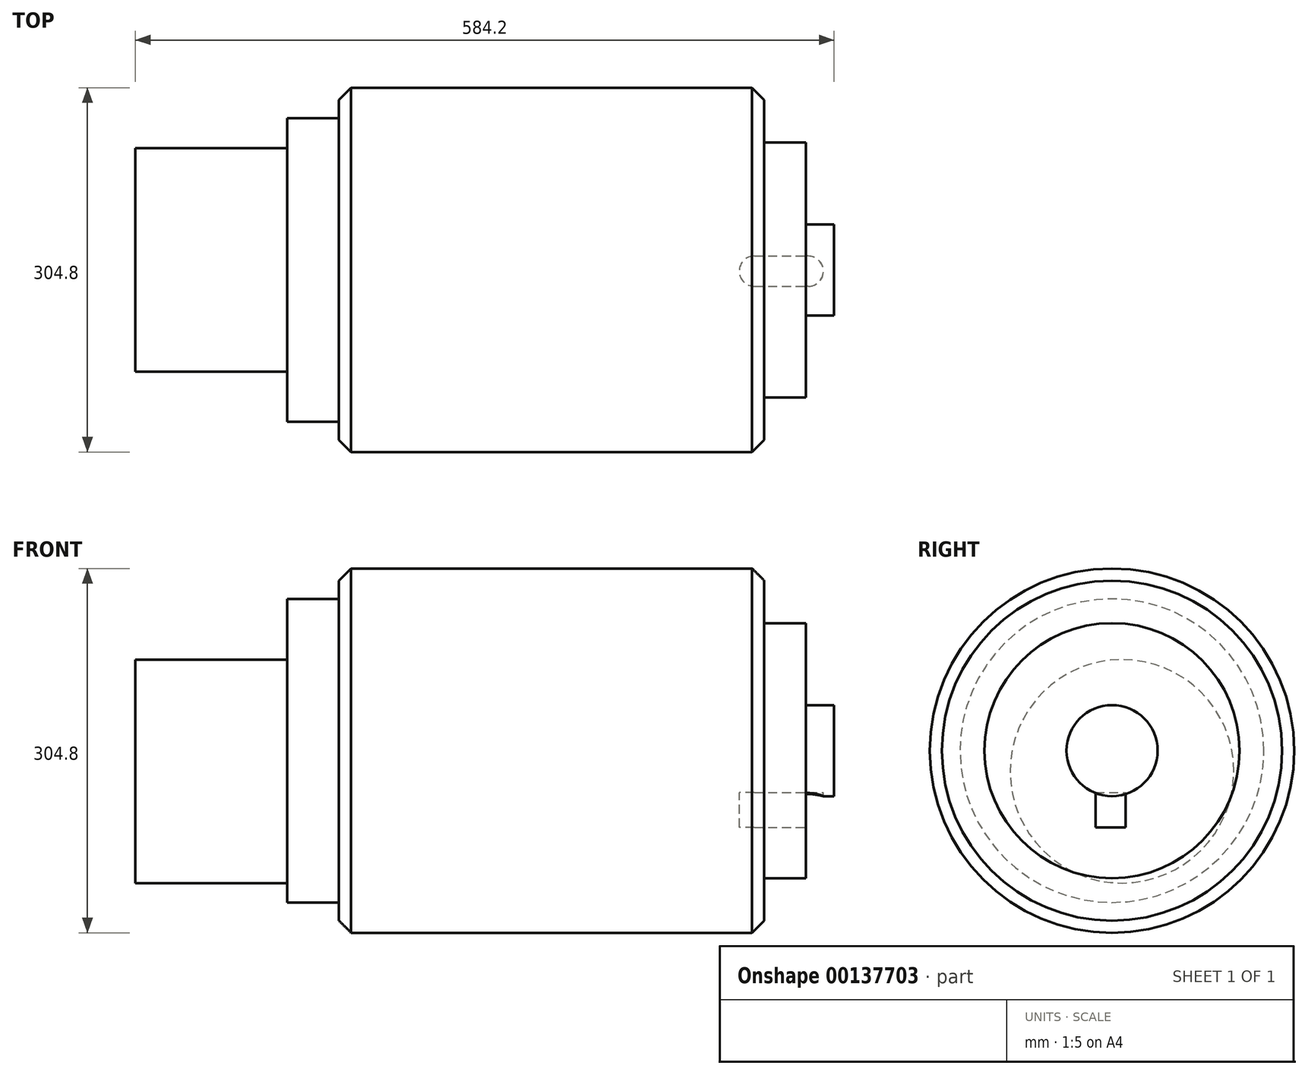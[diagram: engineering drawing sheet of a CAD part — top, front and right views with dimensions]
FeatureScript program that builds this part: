
annotation { "Feature Type Name" : "Feature", "Feature Type Description" : "" }
export const myFeature = defineFeature(function(context is Context, id is Id, definition is map)
    precondition{}
    {
        {
            var Q0;
            Q0=qCreatedBy(makeId("Front.planeOp"),FACE);
            var sketch = newSketch(context, id + "F0", { "sketchPlane" : qUnion([Q0])});
            skLineSegment(sketch, "E0", {"start": v(0, 0) * mm, "end": v(457.2, 0) * mm});
            skLineSegment(sketch, "E1", {"start": v(457.2, 0) * mm, "end": v(457.2, 38.1) * mm});
            skLineSegment(sketch, "E2", {"start": v(457.2, 38.1) * mm, "end": v(433.52, 38.1) * mm});
            skLineSegment(sketch, "E3", {"start": v(433.52, 38.1) * mm, "end": v(433.52, 106.68) * mm});
            skLineSegment(sketch, "E4", {"start": v(433.52, 106.68) * mm, "end": v(398.78, 106.68) * mm});
            skLineSegment(sketch, "E5", {"start": v(398.78, 106.68) * mm, "end": v(398.78, 152.4) * mm});
            skLineSegment(sketch, "E6", {"start": v(398.78, 152.4) * mm, "end": v(43.18, 152.4) * mm});
            skLineSegment(sketch, "E7", {"start": v(43.18, 152.4) * mm, "end": v(43.18, 127) * mm});
            skLineSegment(sketch, "E8", {"start": v(43.18, 127) * mm, "end": v(0, 127) * mm});
            skLineSegment(sketch, "E9", {"start": v(0, 127) * mm, "end": v(0, 0) * mm});
            skSolve(sketch);
        }
        {
            var Q0;
            Q0=makeQuery(id+"F0.imprint","IMPRINT",FACE,{"disambiguationData":[TD([[makeQuery(id+"F0.imprint","IMPRINT",EDGE,{"derivedFrom":sQuery(id+"F0.wireOp",EDGE,"E0")}),1.0]])]});
            var Q1;
            Q1=sQuery(id+"F0.wireOp",EDGE,"E0");
            revolve(context, id + "F1", {"entities" : qUnion([Q0]), "axis" : qUnion([Q1]), "revolveType" : RevolveType.FULL});
        }
        {
            var Q0;
            Q0=qCreatedBy(makeId("Top.planeOp"),FACE);
            var sketch = newSketch(context, id + "F2", { "sketchPlane" : qUnion([Q0])});
            skLineSegment(sketch, "E10", {"start": v(390.59, 11.49) * mm, "end": v(435.6, 11.49) * mm});
            skArc(sketch, "E11", {"start": v(435.6, 11.49) * mm, "mid": v(448.27, -1.17) * mm, "end": v(435.6, -13.83) * mm});
            skArc(sketch, "E12", {"start": v(390.59, 11.49) * mm, "mid": v(377.93, -1.17) * mm, "end": v(390.59, -13.83) * mm});
            skLineSegment(sketch, "E13", {"start": v(390.59, -13.83) * mm, "end": v(435.6, -13.83) * mm});
            skSolve(sketch);
        }
        {
            var Q0;
            Q0 = qSketchRegion(id + "F2", true);
            extrude(context, id + "F3", {"entities" : qUnion([Q0]), "operationType" : NewBodyOperationType.REMOVE, "oppositeDirection" : true, "depth" : 64.26 * mm, "hasSecondDirection" : true, "secondDirectionOppositeDirection" : true, "secondDirectionDepth" : 35.13 * mm});
        }
        {
            var Q0;
            Q0=makeQuery(id+"F1.opRevolve","SWEPT_EDGE",EDGE,{"disambiguationData":[OSD([sQuery(id+"F0.wireOp",EDGE,"E6"),sQuery(id+"F0.wireOp",EDGE,"E7")])]});
            var Q1;
            Q1=makeQuery(id+"F1.opRevolve","SWEPT_EDGE",EDGE,{"disambiguationData":[OSD([sQuery(id+"F0.wireOp",EDGE,"E5"),sQuery(id+"F0.wireOp",EDGE,"E6")])]});
            chamfer(context, id + "F4", {"entities" : qUnion([Q0, Q1]), "width" : 10.16 * mm, "tangentPropagation" : true});
        }
        {
            var Q0;
            Q0=makeQuery(id+"F1.opRevolve","SWEPT_FACE",FACE,{"disambiguationData":[OSD([sQuery(id+"F0.wireOp",EDGE,"E9")])]});
            var sketch = newSketch(context, id + "F5", { "sketchPlane" : qUnion([Q0])});
            skCircle(sketch, "E14", {"center": v(-8.35, -17.3) * mm, "radius": 93.5 * mm});
            skSolve(sketch);
        }
        {
            var Q0;
            Q0 = qSketchRegion(id + "F5", true);
            extrude(context, id + "F6", {"entities" : qUnion([Q0]), "operationType" : NewBodyOperationType.ADD, "depth" : 127 * mm});
        }
    });
